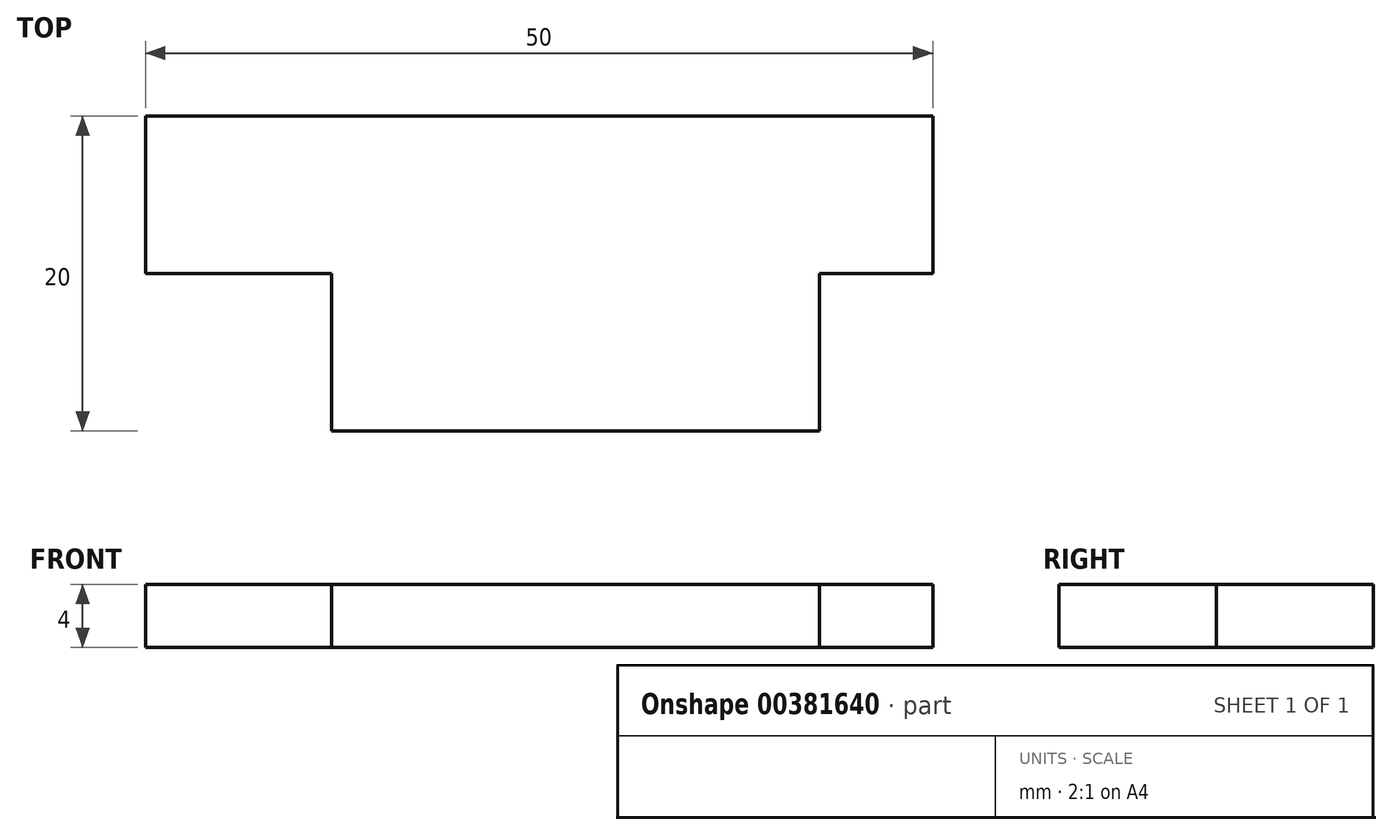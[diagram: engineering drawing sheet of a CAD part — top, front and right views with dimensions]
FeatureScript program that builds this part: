
annotation { "Feature Type Name" : "Feature", "Feature Type Description" : "" }
export const myFeature = defineFeature(function(context is Context, id is Id, definition is map)
    precondition{}
    {
        {
            var Q0;
            Q0=qCreatedBy(makeId("Top.planeOp"),FACE);
            var sketch = newSketch(context, id + "F0", { "sketchPlane" : qUnion([Q0])});
            skLineSegment(sketch, "E0.bottom", {"start": v(-25, 10) * mm, "end": v(25, 10) * mm});
            skLineSegment(sketch, "E0.top", {"start": v(-13.2, -10) * mm, "end": v(17.8, -10) * mm});
            skLineSegment(sketch, "E0.left", {"start": v(-25, 10) * mm, "end": v(-25, 0) * mm});
            skLineSegment(sketch, "E0.right", {"start": v(25, 10) * mm, "end": v(25, 0) * mm});
            skPoint(sketch, "E0.middle", {"position": v(0, 0) * mm});
            skLineSegment(sketch, "E1.top", {"start": v(-25, 0) * mm, "end": v(-13.2, 0) * mm});
            skLineSegment(sketch, "E1.right", {"start": v(-13.2, -10) * mm, "end": v(-13.2, 0) * mm});
            skLineSegment(sketch, "E2.top", {"start": v(25, 0) * mm, "end": v(17.8, 0) * mm});
            skLineSegment(sketch, "E2.right", {"start": v(17.8, -10) * mm, "end": v(17.8, 0) * mm});
            skPoint(sketch, "E3.orphan", {"position": v(-25, -10) * mm});
            skPoint(sketch, "E4.orphan", {"position": v(25, -10) * mm});
            skSolve(sketch);
        }
        {
            var Q0;
            Q0=makeQuery(id+"F0.imprint","IMPRINT",FACE,{"disambiguationData":[TD([[makeQuery(id+"F0.imprint","IMPRINT",EDGE,{"derivedFrom":sQuery(id+"F0.wireOp",EDGE,"E0.bottom")}),-1.0]])]});
            extrude(context, id + "F1", {"entities" : qUnion([Q0]), "depth" : 4 * mm});
        }
    });
